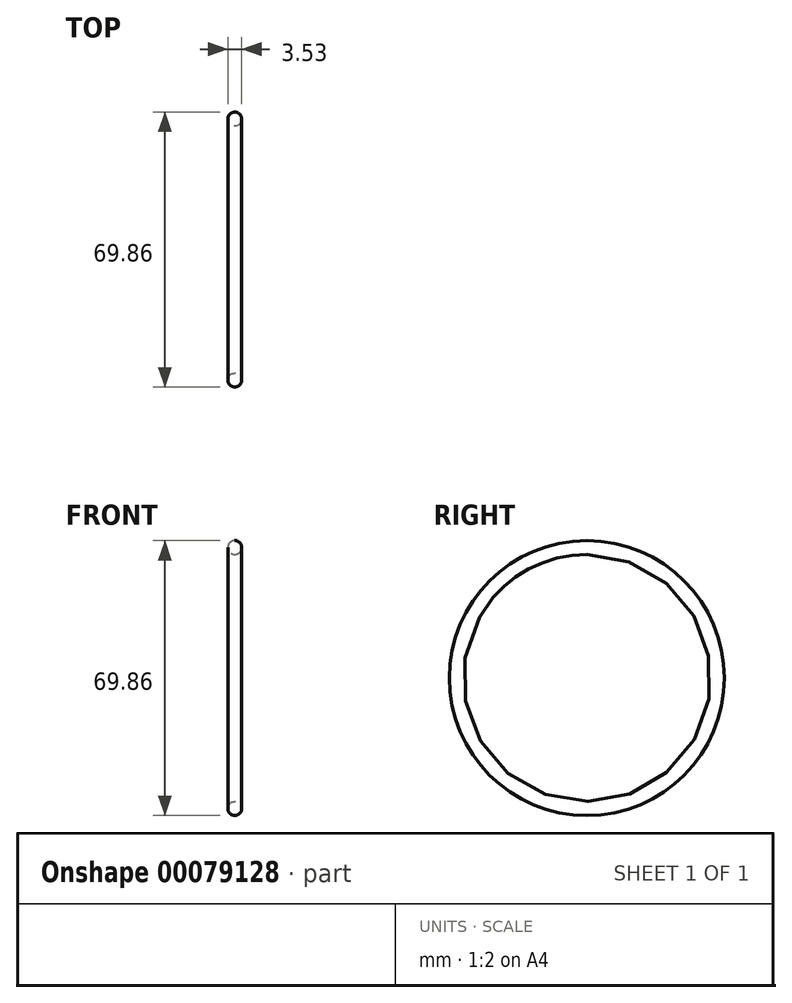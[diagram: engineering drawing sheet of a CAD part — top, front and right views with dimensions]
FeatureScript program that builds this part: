
annotation { "Feature Type Name" : "Feature", "Feature Type Description" : "" }
export const myFeature = defineFeature(function(context is Context, id is Id, definition is map)
    precondition{}
    {
        {
            var Q0;
            Q0=qCreatedBy(makeId("Front.planeOp"),FACE);
            var sketch = newSketch(context, id + "F0", { "sketchPlane" : qUnion([Q0])});
            skLineSegment(sketch, "E0", {"start": v(-11.13, 0) * mm, "end": v(44.8, 0) * mm});
            skCircle(sketch, "E1", {"center": v(9.77, 33.16) * mm, "radius": 1.77 * mm});
            skSolve(sketch);
        }
        {
            var Q0;
            Q0 = qSketchRegion(id + "F0", true);
            var Q1;
            Q1=sQuery(id+"F0.wireOp",EDGE,"E0");
            revolve(context, id + "F1", {"entities" : qUnion([Q0]), "axis" : qUnion([Q1]), "revolveType" : RevolveType.FULL});
        }
    });
